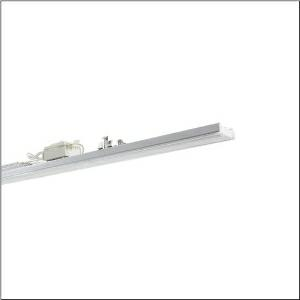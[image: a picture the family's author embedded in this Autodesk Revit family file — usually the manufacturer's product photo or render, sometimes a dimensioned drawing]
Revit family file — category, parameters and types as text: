
# Revit family: licross_r__11_recessed_mo_51te1edv4e5g_50c7
name_source: partatom
category: Lighting Fixtures
units: mm (PartAtom-declared; Revit-internal decimal feet)

## family parameters
Cut with Voids When Loaded = No
Host = Face
Light Source = No
Part Type = Normal
Room Calculation Point = No
Round Connector Dimension = Use Diameter
Shared = No

## types (1)
- --- (1 x LED, 14850 lm, 84.1 W, 4000K)
    Apparent Load = 84 VA
    CIE Flux Codes = 85 95 99 100 100
    Color Rendering = 80
    Color Temperature = 4000K
    Default Elevation = 1800 mm
    Description = Licross® 11 Recessed MO, luminaire insert, of sheet steel, galvanised, coil coated, white, length: 2.250mm, width: 66mm, height: 67mm, LED rated luminous flux: 14.850lm, light colour: 840, control gear: DALI 2, with plug, 5-pole, with phase selection, mains connection: 220..240V, AC, 50/60Hz, rated input power: 84W, halogen-free wiring, primary light control with lens, of plastic, primary optical cover: cover, of PMMA, light emission: direct distribution, primary light characteristic: symmetric, protection rating (complete): IP54, insulation class (complete): insulation class I (protective earthing), certification: CE, ENEC, VDE, UKCA, protection symbol: D if used in an environment with non-conductive dust loads with corresponding accessories, impact resistance: IK06, permissible ambient temperature for indoor applications: -25..+35°C, corresponds to IFS (International Featured Standards) requirements for safety and quality in the food industry, reducing of maximum allowable ambient temperature of 5°C with ceiling mounting, LABS conformity tested according to VDMA 24364:2018-05, packaging unit: 1 piece
    Height = 58 mm
    Lamp = 1 x LED
    Lamp Light Flux = 14850 lm
    Lamp Power = 84.1 W
    Lamp count = 1
    Length = 2250 mm
    Luminous efficacy = 177 lm/W
    Manufacturer = Siteco
    ModVariant = No
    Model = 51TE1EDV4E5G
    Mounting Place = Ceiling
    Mounting Type = Pendant
    Number of Poles = 1
    OnlyDefault = Yes
    Power Factor = 1
    Product Name = Licross® 11 Recessed MO
    Product group = luminaire insert
    ProductGroupID = 902
    Protection Class = Protection class I
    Protection Degree = IP 54
    RLX_Detail_Level = 1
    RLX_Emergency_Light_Flux = 0 lm
    RLX_Emergency_Type = 0
    RLX_Emergency_Type_DB = No
    RlxData = <blob elided: 29569 chars, md5=9d7b4148>
    Socket = socket
    Standby Power = 0 W
    System Light Flux = 14850 lm
    System Power = 84 W
    Type Comments = factory setting: luminous flux: 100 % | dim-lin: 254 | 378 mA
    Type Image = l_1296930.jpg
    URL = http://relux.com
    VarID = @adj_095714
    Voltage = 0 V
    Weight = 0.00 kg
    Width = 66 mm

## geometry (parser evidence)
native form markers: Blend x4, Sweep x10
no freeform markers — native parametric forms only
